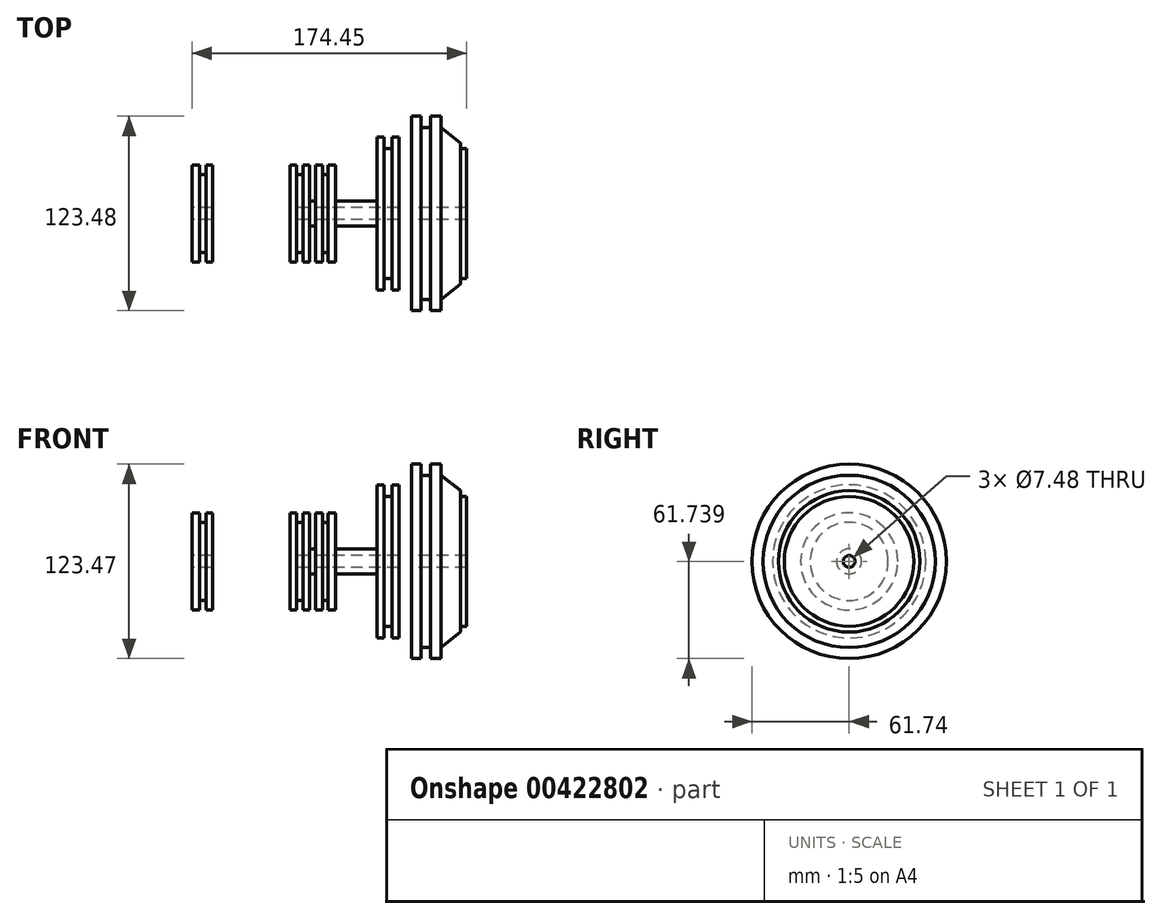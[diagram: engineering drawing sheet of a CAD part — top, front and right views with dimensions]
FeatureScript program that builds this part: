
annotation { "Feature Type Name" : "Feature", "Feature Type Description" : "" }
export const myFeature = defineFeature(function(context is Context, id is Id, definition is map)
    precondition{}
    {
        {
            var Q0;
            Q0=qCreatedBy(makeId("Front.planeOp"),FACE);
            var sketch = newSketch(context, id + "F0", { "sketchPlane" : qUnion([Q0])});
            skLineSegment(sketch, "E0", {"start": v(-154.34, 0) * mm, "end": v(0, 0) * mm});
            skLineSegment(sketch, "E1", {"start": v(-162.76, -3.74) * mm, "end": v(55.19, -3.74) * mm});
            skLineSegment(sketch, "E2", {"start": v(-139.37, 0) * mm, "end": v(-139.37, 27.13) * mm});
            skLineSegment(sketch, "E3", {"start": v(-139.37, 27.13) * mm, "end": v(-134.7, 27.13) * mm});
            skLineSegment(sketch, "E4", {"start": v(-134.7, 27.13) * mm, "end": v(-134.7, 21.05) * mm});
            skLineSegment(sketch, "E5", {"start": v(-134.7, 21.05) * mm, "end": v(-130.49, 21.05) * mm});
            skLineSegment(sketch, "E6", {"start": v(-130.49, 21.05) * mm, "end": v(-130.49, 27.13) * mm});
            skLineSegment(sketch, "E7", {"start": v(-130.49, 27.13) * mm, "end": v(-126.28, 27.13) * mm});
            skLineSegment(sketch, "E8", {"start": v(-126.28, 27.13) * mm, "end": v(-126.28, 0) * mm});
            skLineSegment(sketch, "E9", {"start": v(-126.28, 0) * mm, "end": v(-139.37, 0) * mm});
            skLineSegment(sketch, "E10", {"start": v(-77.17, 0) * mm, "end": v(-77.17, 27.13) * mm});
            skLineSegment(sketch, "E11", {"start": v(-77.17, 27.13) * mm, "end": v(-72.96, 27.13) * mm});
            skLineSegment(sketch, "E12", {"start": v(-72.96, 27.13) * mm, "end": v(-72.96, 21.05) * mm});
            skLineSegment(sketch, "E13", {"start": v(-72.96, 21.05) * mm, "end": v(-68.75, 21.05) * mm});
            skLineSegment(sketch, "E14", {"start": v(-68.75, 21.05) * mm, "end": v(-68.75, 27.13) * mm});
            skLineSegment(sketch, "E15", {"start": v(-68.75, 27.13) * mm, "end": v(-64.54, 27.13) * mm});
            skLineSegment(sketch, "E16", {"start": v(-64.54, 27.13) * mm, "end": v(-64.54, 0) * mm});
            skLineSegment(sketch, "E17", {"start": v(-64.54, 0) * mm, "end": v(-77.17, 0) * mm});
            skLineSegment(sketch, "E18", {"start": v(-60.8, 0) * mm, "end": v(-60.8, 27.13) * mm});
            skLineSegment(sketch, "E19", {"start": v(-60.8, 27.13) * mm, "end": v(-56.6, 27.13) * mm});
            skLineSegment(sketch, "E20", {"start": v(-56.6, 27.13) * mm, "end": v(-56.6, 21.05) * mm});
            skLineSegment(sketch, "E21", {"start": v(-56.6, 21.05) * mm, "end": v(-52.85, 21.05) * mm});
            skLineSegment(sketch, "E22", {"start": v(-52.85, 21.05) * mm, "end": v(-52.85, 27.13) * mm});
            skLineSegment(sketch, "E23", {"start": v(-52.85, 27.13) * mm, "end": v(-48.17, 27.13) * mm});
            skLineSegment(sketch, "E24", {"start": v(-48.17, 27.13) * mm, "end": v(-48.17, 0) * mm});
            skLineSegment(sketch, "E25", {"start": v(-48.17, 0) * mm, "end": v(-60.8, 0) * mm});
            skLineSegment(sketch, "E26", {"start": v(-48.17, 4.2) * mm, "end": v(-21.98, 4.2) * mm});
            skLineSegment(sketch, "E27", {"start": v(-21.98, 4.2) * mm, "end": v(-21.98, 44.9) * mm});
            skLineSegment(sketch, "E28", {"start": v(-21.98, 4.2) * mm, "end": v(-21.98, 0) * mm});
            skLineSegment(sketch, "E29", {"start": v(-21.98, 0) * mm, "end": v(-21.98, 44.9) * mm});
            skLineSegment(sketch, "E30", {"start": v(-21.98, 44.9) * mm, "end": v(-17.3, 44.9) * mm});
            skLineSegment(sketch, "E31", {"start": v(-17.3, 44.9) * mm, "end": v(-17.3, 37.42) * mm});
            skLineSegment(sketch, "E32", {"start": v(-17.3, 37.42) * mm, "end": v(-12.16, 37.42) * mm});
            skLineSegment(sketch, "E33", {"start": v(-12.16, 37.42) * mm, "end": v(-12.16, 44.9) * mm});
            skLineSegment(sketch, "E34", {"start": v(-12.16, 44.9) * mm, "end": v(-7.95, 44.9) * mm});
            skLineSegment(sketch, "E35", {"start": v(-7.95, 44.9) * mm, "end": v(-7.95, 0) * mm});
            skLineSegment(sketch, "E36", {"start": v(-7.95, 0) * mm, "end": v(-21.98, 0) * mm});
            skLineSegment(sketch, "E37", {"start": v(0, 0) * mm, "end": v(84.65, 0) * mm});
            skLineSegment(sketch, "E38", {"start": v(55.19, -3.74) * mm, "end": v(115.52, -3.74) * mm});
            skLineSegment(sketch, "E39", {"start": v(0, 0) * mm, "end": v(0, 58) * mm});
            skLineSegment(sketch, "E40", {"start": v(0, 58) * mm, "end": v(6.08, 58) * mm});
            skLineSegment(sketch, "E41", {"start": v(6.08, 58) * mm, "end": v(6.08, 50.98) * mm});
            skLineSegment(sketch, "E42", {"start": v(6.08, 50.98) * mm, "end": v(12.16, 50.98) * mm});
            skLineSegment(sketch, "E43", {"start": v(12.16, 50.98) * mm, "end": v(12.16, 58) * mm});
            skLineSegment(sketch, "E44", {"start": v(12.16, 58) * mm, "end": v(18.7, 58) * mm});
            skLineSegment(sketch, "E45", {"start": v(18.7, 58) * mm, "end": v(18.7, 50.98) * mm});
            skLineSegment(sketch, "E46", {"start": v(18.7, 50.98) * mm, "end": v(31.34, 41.16) * mm});
            skLineSegment(sketch, "E47", {"start": v(31.34, 41.16) * mm, "end": v(31.34, 37.42) * mm});
            skLineSegment(sketch, "E48", {"start": v(31.34, 37.42) * mm, "end": v(35.08, 37.42) * mm});
            skLineSegment(sketch, "E49", {"start": v(35.08, 37.42) * mm, "end": v(35.08, 0) * mm});
            skLineSegment(sketch, "E50", {"start": v(35.08, 0) * mm, "end": v(0, 0) * mm});
            skLineSegment(sketch, "E51", {"start": v(35.08, 0) * mm, "end": v(35.08, 37.42) * mm});
            skLineSegment(sketch, "E52", {"start": v(35.08, 37.42) * mm, "end": v(35.08, 41.16) * mm});
            skLineSegment(sketch, "E53", {"start": v(35.08, 41.16) * mm, "end": v(47.7, 50.98) * mm});
            skLineSegment(sketch, "E54", {"start": v(47.7, 50.98) * mm, "end": v(47.7, 58) * mm});
            skLineSegment(sketch, "E55", {"start": v(47.7, 58) * mm, "end": v(55.19, 58) * mm});
            skLineSegment(sketch, "E56", {"start": v(55.19, 58) * mm, "end": v(55.19, 50.98) * mm});
            skLineSegment(sketch, "E57", {"start": v(55.19, 50.98) * mm, "end": v(59.4, 50.98) * mm});
            skLineSegment(sketch, "E58", {"start": v(59.4, 50.98) * mm, "end": v(59.4, 58) * mm});
            skLineSegment(sketch, "E59", {"start": v(59.4, 58) * mm, "end": v(65.94, 58) * mm});
            skLineSegment(sketch, "E60", {"start": v(65.94, 58) * mm, "end": v(65.94, 50.98) * mm});
            skLineSegment(sketch, "E61", {"start": v(65.94, 50.98) * mm, "end": v(65.94, 0) * mm});
            skLineSegment(sketch, "E62", {"start": v(65.94, 0) * mm, "end": v(35.08, 0) * mm});
            skLineSegment(sketch, "E63", {"start": v(-48.17, 4.2) * mm, "end": v(-126.28, 4.2) * mm});
            skLineSegment(sketch, "E64", {"start": v(-126.28, 4.2) * mm, "end": v(-126.28, 0) * mm});
            skLineSegment(sketch, "E65", {"start": v(-126.28, 0) * mm, "end": v(-21.98, 0) * mm});
            skLineSegment(sketch, "E66", {"start": v(-21.98, 4.2) * mm, "end": v(0, 4.2) * mm});
            skLineSegment(sketch, "E67", {"start": v(0, 4.2) * mm, "end": v(0, 0) * mm});
            skLineSegment(sketch, "E68", {"start": v(0, 0) * mm, "end": v(-48.17, 0) * mm});
            skSolve(sketch);
        }
        {
            var Q0;
            {var subQ3=sQuery(id+"F0.wireOp",EDGE,"E26");Q0=makeQuery(id+"F0.imprint","IMPRINT",FACE,{"disambiguationData":[TD([[makeQuery(id+"F0.imprint","IMPRINT",EDGE,{"derivedFrom":subQ3}),-1.0]])]});}
            var Q1;
            {var subQ5=sQuery(id+"F0.wireOp",EDGE,"E67");Q1=makeQuery(id+"F0.imprint","IMPRINT",FACE,{"disambiguationData":[TD([[makeQuery(id+"F0.imprint","IMPRINT",EDGE,{"derivedFrom":subQ5}),-1.0]])]});}
            var Q2;
            {var subQ0=sQuery(id+"F0.wireOp",EDGE,"E65");var subQ1=sQuery(id+"F0.wireOp",EDGE,"E16");var subQ2=makeQuery(id+"F0.imprint","INTERSECT",VERTEX,{"derivedFrom":[subQ1,subQ0]});Q2=makeQuery(id+"F0.imprint","IMPRINT",FACE,{"disambiguationData":[TD([[makeQuery(id+"F0.imprint","IMPRINT",EDGE,{"disambiguationData":[TD([[subQ2,1.0]])],"derivedFrom":subQ1}),1.0]])]});}
            var Q3;
            {var subQ0=sQuery(id+"F0.wireOp",EDGE,"E65");var subQ1=sQuery(id+"F0.wireOp",EDGE,"E18");var subQ2=makeQuery(id+"F0.imprint","INTERSECT",VERTEX,{"derivedFrom":[subQ1,subQ0]});Q3=makeQuery(id+"F0.imprint","IMPRINT",FACE,{"disambiguationData":[TD([[makeQuery(id+"F0.imprint","IMPRINT",EDGE,{"disambiguationData":[TD([[subQ2,-1.0]])],"derivedFrom":subQ1}),-1.0]])]});}
            var Q4;
            {var subQ0=sQuery(id+"F0.wireOp",EDGE,"E65");var subQ1=sQuery(id+"F0.wireOp",EDGE,"E10");var subQ2=makeQuery(id+"F0.imprint","INTERSECT",VERTEX,{"derivedFrom":[subQ1,subQ0]});Q4=makeQuery(id+"F0.imprint","IMPRINT",FACE,{"disambiguationData":[TD([[makeQuery(id+"F0.imprint","IMPRINT",EDGE,{"disambiguationData":[TD([[subQ2,-1.0]])],"derivedFrom":subQ1}),-1.0]])]});}
            var Q5;
            {var subQ5=sQuery(id+"F0.wireOp",EDGE,"E64");Q5=makeQuery(id+"F0.imprint","IMPRINT",FACE,{"disambiguationData":[TD([[makeQuery(id+"F0.imprint","IMPRINT",EDGE,{"derivedFrom":subQ5}),1.0]])]});}
            var Q6;
            {var subQ0=sQuery(id+"F0.wireOp",EDGE,"E30");Q6=makeQuery(id+"F0.imprint","IMPRINT",FACE,{"disambiguationData":[TD([[makeQuery(id+"F0.imprint","IMPRINT",EDGE,{"derivedFrom":subQ0}),-1.0]])]});}
            var Q7;
            {var subQ3=sQuery(id+"F0.wireOp",EDGE,"E68");var subQ5=sQuery(id+"F0.wireOp",EDGE,"E35");var subQ6=makeQuery(id+"F0.imprint","INTERSECT",VERTEX,{"derivedFrom":[subQ5,subQ3]});Q7=makeQuery(id+"F0.imprint","IMPRINT",FACE,{"disambiguationData":[TD([[makeQuery(id+"F0.imprint","IMPRINT",EDGE,{"disambiguationData":[TD([[subQ6,1.0]])],"derivedFrom":subQ5}),-1.0]])]});}
            var Q8;
            {var subQ0=sQuery(id+"F0.wireOp",EDGE,"E19");Q8=makeQuery(id+"F0.imprint","IMPRINT",FACE,{"disambiguationData":[TD([[makeQuery(id+"F0.imprint","IMPRINT",EDGE,{"derivedFrom":subQ0}),-1.0]])]});}
            var Q9;
            {var subQ0=sQuery(id+"F0.wireOp",EDGE,"E11");Q9=makeQuery(id+"F0.imprint","IMPRINT",FACE,{"disambiguationData":[TD([[makeQuery(id+"F0.imprint","IMPRINT",EDGE,{"derivedFrom":subQ0}),-1.0]])]});}
            var Q10;
            Q10=makeQuery(id+"F0.imprint","IMPRINT",FACE,{"disambiguationData":[TD([[makeQuery(id+"F0.imprint","IMPRINT",EDGE,{"derivedFrom":sQuery(id+"F0.wireOp",EDGE,"E2")}),-1.0]])]});
            var Q11;
            Q11=makeQuery(id+"F0.imprint","IMPRINT",FACE,{"disambiguationData":[TD([[makeQuery(id+"F0.imprint","IMPRINT",EDGE,{"derivedFrom":sQuery(id+"F0.wireOp",EDGE,"E39")}),-1.0]])]});
            var Q12;
            Q12=makeQuery(id+"F0.imprint","IMPRINT",FACE,{"disambiguationData":[TD([[makeQuery(id+"F0.imprint","IMPRINT",EDGE,{"derivedFrom":sQuery(id+"F0.wireOp",EDGE,"E51")}),-1.0]])]});
            var Q13;
            Q13=sQuery(id+"F0.wireOp",EDGE,"E1");
            revolve(context, id + "F1", {"entities" : qUnion([Q0, Q1, Q2, Q3, Q4, Q5, Q6, Q7, Q8, Q9, Q10, Q11, Q12]), "axis" : qUnion([Q13]), "revolveType" : RevolveType.FULL});
        }
        {
            var Q0;
            Q0=qCreatedBy(makeId("Front.planeOp"),FACE);
            var sketch = newSketch(context, id + "F2", { "sketchPlane" : qUnion([Q0])});
            skLineSegment(sketch, "E69", {"start": v(-126.4, 15.7) * mm, "end": v(-76.87, 15.7) * mm});
            skLineSegment(sketch, "E70", {"start": v(-126.4, -25.06) * mm, "end": v(-77.18, -25.06) * mm});
            skLineSegment(sketch, "E71", {"start": v(-144.5, -23.25) * mm, "end": v(-33.7, -23.25) * mm});
            skLineSegment(sketch, "E72", {"start": v(-144.5, 13.59) * mm, "end": v(-34.3, 13.59) * mm});
            skSolve(sketch);
        }
        {
            var Q0;
            Q0=sQuery(id+"F2.wireOp",EDGE,"E70");
            var Q1;
            Q1=sQuery(id+"F2.wireOp",EDGE,"E71");
            revolve(context, id + "F3", {"bodyType" : ToolBodyType.SURFACE, "surfaceEntities" : qUnion([Q0]), "axis" : qUnion([Q1]), "revolveType" : RevolveType.FULL});
        }
        {
            var Q0;
            Q0=qCreatedBy(makeId("Front.planeOp"),FACE);
            var sketch = newSketch(context, id + "F4", { "sketchPlane" : qUnion([Q0])});
            skLineSegment(sketch, "E73", {"start": v(-126.7, 16.6) * mm, "end": v(-77.48, 16.6) * mm});
            skLineSegment(sketch, "E74", {"start": v(-144.2, 14.8) * mm, "end": v(-35.2, 14.8) * mm});
            skSolve(sketch);
        }
        {
            var Q0;
            Q0=sQuery(id+"F4.wireOp",EDGE,"E73");
            var Q1;
            Q1=sQuery(id+"F4.wireOp",EDGE,"E74");
            revolve(context, id + "F5", {"bodyType" : ToolBodyType.SURFACE, "surfaceEntities" : qUnion([Q0]), "axis" : qUnion([Q1]), "revolveType" : RevolveType.FULL});
        }
        {
            var Q0;
            Q0=qCreatedBy(makeId("Front.planeOp"),FACE);
            var sketch = newSketch(context, id + "F6", { "sketchPlane" : qUnion([Q0])});
            skLineSegment(sketch, "E75", {"start": v(-48.2, 10.87) * mm, "end": v(-21.92, 10.87) * mm});
            skLineSegment(sketch, "E76", {"start": v(-61.17, 8.45) * mm, "end": v(-2.9, 8.45) * mm});
            skSolve(sketch);
        }
        {
            var Q0;
            Q0=sQuery(id+"F6.wireOp",EDGE,"E75");
            var Q1;
            Q1=sQuery(id+"F6.wireOp",EDGE,"E76");
            revolve(context, id + "F7", {"bodyType" : ToolBodyType.SURFACE, "surfaceEntities" : qUnion([Q0]), "axis" : qUnion([Q1]), "revolveType" : RevolveType.FULL});
        }
        {
            var Q0;
            Q0=qCreatedBy(makeId("Front.planeOp"),FACE);
            var sketch = newSketch(context, id + "F8", { "sketchPlane" : qUnion([Q0])});
            skLineSegment(sketch, "E77", {"start": v(-48.2, -17.81) * mm, "end": v(-22.53, -17.81) * mm});
            skLineSegment(sketch, "E78", {"start": v(-61.48, -15.4) * mm, "end": v(-4.71, -15.4) * mm});
            skSolve(sketch);
        }
        {
            var Q0;
            Q0=sQuery(id+"F8.wireOp",EDGE,"E77");
            var Q1;
            Q1=sQuery(id+"F8.wireOp",EDGE,"E78");
            revolve(context, id + "F9", {"bodyType" : ToolBodyType.SURFACE, "surfaceEntities" : qUnion([Q0]), "axis" : qUnion([Q1]), "revolveType" : RevolveType.FULL});
        }
        {
            var Q0;
            Q0=qCreatedBy(makeId("Front.planeOp"),FACE);
            var sketch = newSketch(context, id + "F10", { "sketchPlane" : qUnion([Q0])});
            skLineSegment(sketch, "E79", {"start": v(-8.34, 25.06) * mm, "end": v(0, 25.06) * mm});
            skLineSegment(sketch, "E80", {"start": v(-25.85, 19.93) * mm, "end": v(70.46, 19.93) * mm});
            skSolve(sketch);
        }
        {
            var Q0;
            Q0=sQuery(id+"F10.wireOp",EDGE,"E79");
            var Q1;
            Q1=sQuery(id+"F10.wireOp",EDGE,"E80");
            revolve(context, id + "F11", {"bodyType" : ToolBodyType.SURFACE, "surfaceEntities" : qUnion([Q0]), "axis" : qUnion([Q1]), "revolveType" : RevolveType.FULL});
        }
        {
            var Q0;
            Q0=qCreatedBy(makeId("Front.planeOp"),FACE);
            var sketch = newSketch(context, id + "F12", { "sketchPlane" : qUnion([Q0])});
            skLineSegment(sketch, "E81", {"start": v(-8.28, -32.46) * mm, "end": v(0, -32.46) * mm});
            skLineSegment(sketch, "E82", {"start": v(-25.68, -26.98) * mm, "end": v(82.9, -26.98) * mm});
            skSolve(sketch);
        }
        {
            var Q0;
            Q0=sQuery(id+"F12.wireOp",EDGE,"E81");
            var Q1;
            Q1=sQuery(id+"F12.wireOp",EDGE,"E82");
            revolve(context, id + "F13", {"bodyType" : ToolBodyType.SURFACE, "surfaceEntities" : qUnion([Q0]), "axis" : qUnion([Q1]), "revolveType" : RevolveType.FULL});
        }
    });
